# Revit family: DAIKIN_VRV_Indoor Unit_Duct_M.S.P._FXSQ-PAVS_FXSQ50PAVS
name_source: partatom
category: Оборудование
units: mm (PartAtom-declared; Revit-internal decimal feet)

## family parameters
Всегда вертикально = Да
Заголовок OmniClass = Split System Air Conditioning Units
Классификация = Насос
На основе рабочей плоскости = Нет
Номер OmniClass = 23.75.10.24.21.27.27
Общий = Нет
При загрузке вырезать с полостями = Нет
Размер круглого соединителя = Использовать радиус
Сохранять ориентацию аннотаций = Нет
Тип детали = Нормальный
Точка принадлежности помещению = Да

## types (1)
- FXSQ50PAVS
    Clearance Bottom = 300 мм
    Clearance Front = 450 мм
    Clearance Left = 0 мм
    Clearance Rear = 0 мм
    Clearance Right = 0 мм
    Clearance Top = 20 мм
    Depth = 1000 мм
    Drain Pipe Size = 25.0 мм
    Fan Drive = Direct Drive
    Fan Type = Sirocco Fan
    Frequency_50Hz = 50 Гц
    Gas Pipe Size = 12.7 мм
    Heat Exchanger Type = Cross Fin Coil
    Height = 245 мм
    IfcExportAs = IfcUnitaryEquipmentType
    IfcExportType = AIRCONDITIONINGUNIT
    IfcVersion = 0
    Liquid Pipe Size = 6.4 мм
    Load Classification = HVAC
    Material_Casing = DAIKIN_GalvanizedSteel_Casing_indoorunit
    Maximum Airflow = 1020.00 м³/ч
    Maximum External Static Pressure = 150.00 Па
    Maximum Fuse Amps_50Hz = 16.0 А
    Median Airflow = 870.00 м³/ч
    Minimum Airflow = 690.00 м³/ч
    Minimum Circuit Amps_50Hz = 1.3 А
    Minimum External Static Pressure = 50.00 Па
    Nominal Cooling Capacity = 5.600 кВт
    Nominal Heating Capacity = 6.300 кВт
    Phase_50Hz = 1
    Power Input (Cooling) = 0.164 кВт
    Power Input (Heating) = 0.159 кВт
    RA Duct Size Height = 208 мм
    RA Duct Size Width = 952 мм
    Refrigerant Type = R410A
    SA Duct Size Height = 176 мм
    SA Duct Size Width = 792 мм
    Series = VRV Fan Coil Unit
    Sound Power Level_H speed (dB) = 62
    Sound Pressure Level_H speed (dBA) = 34
    Sound Pressure Level_L speed (dBA) = 29
    Sound Pressure Level_M speed (dBA) = 0
    Uniclass2015Code = Pr_70_65_03_94
    Uniclass2015Title = Variable refrigerant flow units
    Uniclass2015Version = Products v1.30
    Unit Mass Weight = 35.00 кг
    Unit Type = Middle Static Pressure Duct Type
    Version = ver.1.0
    Voltage_50Hz = 220 В
    Voltage_comment_50Hz = 220-240
    Width = 800 мм
    h*** = 0 мм
    ld_drainpipe = 553 мм
    ld_gaspipe = 565 мм
    ld_liquidpipe = 569 мм
    ld_mountinghole = 1038 мм
    ld_power = 500 мм
    lh_RA = 123 мм
    lh_SA = 138 мм
    lh_antena = 24 мм
    lh_drainpipe = 207 мм
    lh_gaspipe = 183 мм
    lh_liquidpipe = 136 мм
    lh_mountinghole = 222 мм
    lh_mountinghole1 = 222 мм
    lh_power = 60 мм
    lw_RA = 499 мм
    lw_SA = 450 мм
    lw_drainpipe = 300 мм
    lw_gaspipe = 229 мм
    lw_liquidpipe = 179 мм
    lw_mountinghole = 630 мм
    lw_power = 770 мм
    r_Drain Pipe Size = 12.5 мм
    r_Gas Pipe Size = 6.4 мм
    r_Liquid Pipe Size = 3.2 мм
    Группа модели = FXSQ50PAVS
    Изготовитель = Daikin
    Изображение типоразмера = <Нет>
    Отметка по умолчанию = 0 мм
    Стоимость = долл. США0.00
    Тип Предварительно заданный тип IFC = AIRCONDITIONINGUNIT
    Экспорт типа в IFC как = IfcUnitaryEquipmentType

## geometry (parser evidence)
native form markers: Sweep x16
no freeform markers — native parametric forms only
